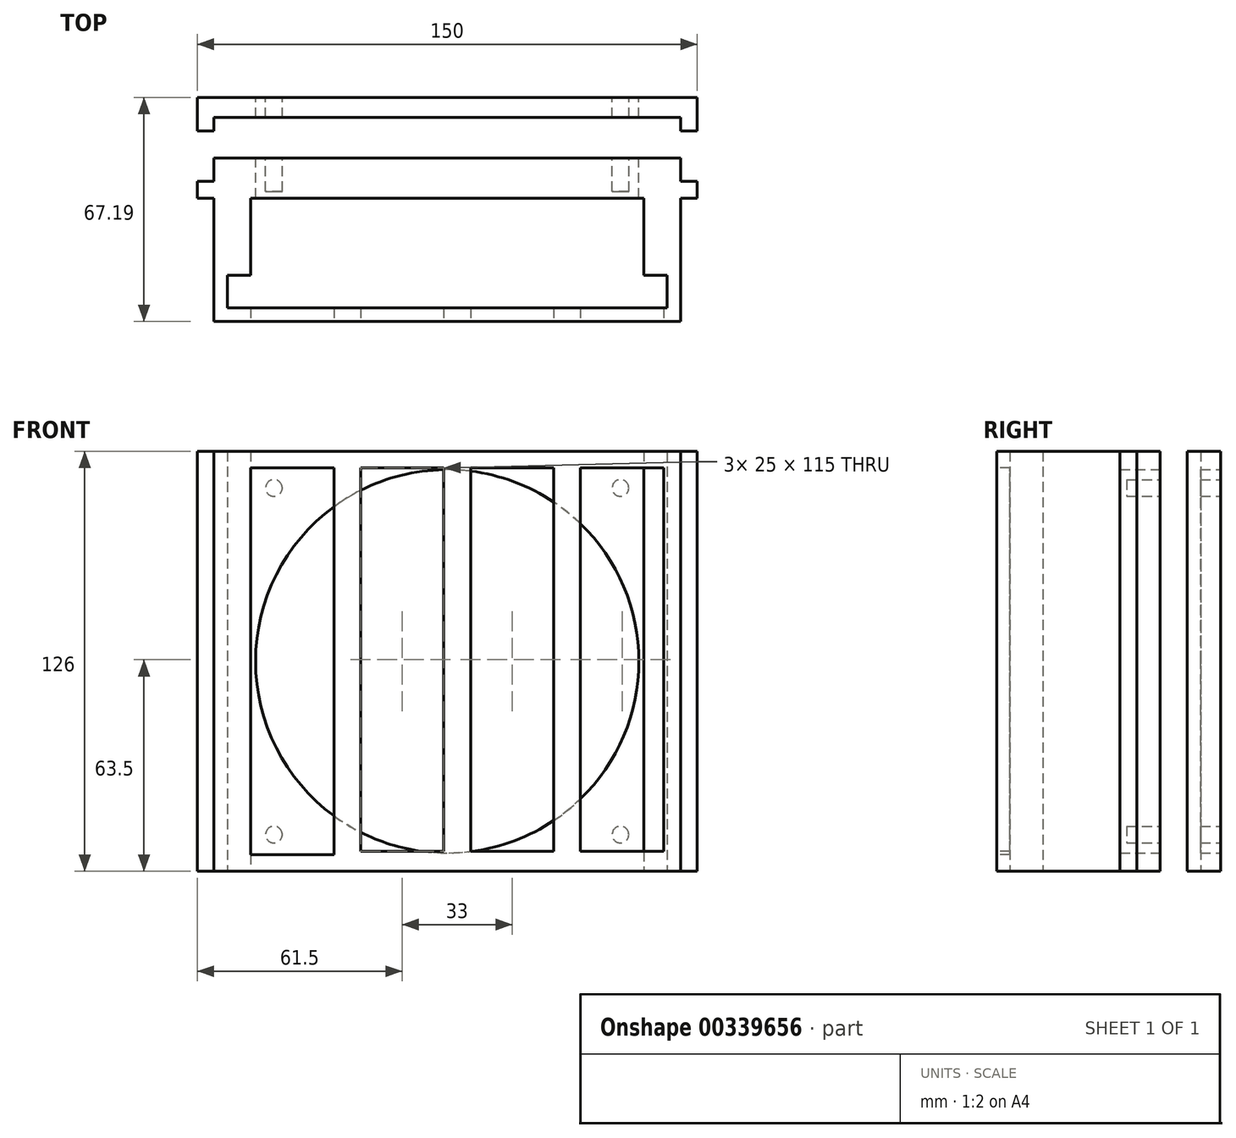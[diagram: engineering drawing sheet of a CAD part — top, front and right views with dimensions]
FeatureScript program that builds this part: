
annotation { "Feature Type Name" : "Feature", "Feature Type Description" : "" }
export const myFeature = defineFeature(function(context is Context, id is Id, definition is map)
    precondition{}
    {
        {
            var Q0;
            Q0=qCreatedBy(makeId("Top.planeOp"),FACE);
            var sketch = newSketch(context, id + "F0", { "sketchPlane" : qUnion([Q0])});
            skLineSegment(sketch, "E0.bottom", {"start": v(-66, 14) * mm, "end": v(66, 14) * mm});
            skLineSegment(sketch, "E0.top", {"start": v(-66, -19) * mm, "end": v(66, -19) * mm});
            skLineSegment(sketch, "E0.left", {"start": v(-66, 14) * mm, "end": v(-66, -19) * mm});
            skLineSegment(sketch, "E0.right", {"start": v(66, 14) * mm, "end": v(66, -19) * mm});
            skLineSegment(sketch, "E1.bottom", {"start": v(-66, -9.2) * mm, "end": v(-59, -9.2) * mm});
            skLineSegment(sketch, "E1.top", {"start": v(-66, 14) * mm, "end": v(-59, 14) * mm});
            skLineSegment(sketch, "E1.left", {"start": v(-66, -9.2) * mm, "end": v(-66, 14) * mm});
            skLineSegment(sketch, "E1.right", {"start": v(-59, -9.2) * mm, "end": v(-59, 14) * mm});
            skLineSegment(sketch, "E2.bottom", {"start": v(66, -9.2) * mm, "end": v(59, -9.2) * mm});
            skLineSegment(sketch, "E2.top", {"start": v(66, 14) * mm, "end": v(59, 14) * mm});
            skLineSegment(sketch, "E2.left", {"start": v(66, -9.2) * mm, "end": v(66, 14) * mm});
            skLineSegment(sketch, "E2.right", {"start": v(59, -9.2) * mm, "end": v(59, 14) * mm});
            skLineSegment(sketch, "E3.bottom", {"start": v(-70, 26) * mm, "end": v(70, 26) * mm});
            skLineSegment(sketch, "E3.top", {"start": v(-70, -23) * mm, "end": v(70, -23) * mm});
            skLineSegment(sketch, "E3.left", {"start": v(-70, 26) * mm, "end": v(-70, -23) * mm});
            skLineSegment(sketch, "E3.right", {"start": v(70, 26) * mm, "end": v(70, -23) * mm});
            skLineSegment(sketch, "E4.bottom", {"start": v(-75, 14) * mm, "end": v(-70, 14) * mm});
            skLineSegment(sketch, "E4.top", {"start": v(-75, 19) * mm, "end": v(-70, 19) * mm});
            skLineSegment(sketch, "E4.left", {"start": v(-75, 14) * mm, "end": v(-75, 19) * mm});
            skLineSegment(sketch, "E4.right", {"start": v(75, 14) * mm, "end": v(75, 19) * mm});
            skLineSegment(sketch, "E5.trimOffspring", {"start": v(70, 14) * mm, "end": v(75, 14) * mm});
            skLineSegment(sketch, "E6.trimOffspring", {"start": v(70, 19) * mm, "end": v(75, 19) * mm});
            skLineSegment(sketch, "E7.bottom", {"start": v(75, 34.19) * mm, "end": v(-75, 34.19) * mm});
            skLineSegment(sketch, "E7.top", {"start": v(75, 44.19) * mm, "end": v(-75, 44.19) * mm});
            skLineSegment(sketch, "E7.left", {"start": v(75, 34.19) * mm, "end": v(75, 44.19) * mm});
            skLineSegment(sketch, "E7.right", {"start": v(-75, 34.19) * mm, "end": v(-75, 44.19) * mm});
            skLineSegment(sketch, "E8.bottom", {"start": v(70, 34.19) * mm, "end": v(-70, 34.19) * mm});
            skLineSegment(sketch, "E8.top", {"start": v(70, 38.19) * mm, "end": v(-70, 38.19) * mm});
            skLineSegment(sketch, "E8.left", {"start": v(70, 34.19) * mm, "end": v(70, 38.19) * mm});
            skLineSegment(sketch, "E8.right", {"start": v(-70, 34.19) * mm, "end": v(-70, 38.19) * mm});
            skSolve(sketch);
        }
        {
            var Q0;
            Q0=makeQuery(id+"F0.imprint","IMPRINT",FACE,{"disambiguationData":[TD([[makeQuery(id+"F0.imprint","IMPRINT",EDGE,{"derivedFrom":sQuery(id+"F0.wireOp",EDGE,"E0.bottom")}),1.0]])]});
            var Q1;
            Q1=makeQuery(id+"F0.imprint","IMPRINT",FACE,{"disambiguationData":[TD([[makeQuery(id+"F0.imprint","IMPRINT",EDGE,{"derivedFrom":sQuery(id+"F0.wireOp",EDGE,"E1.bottom")}),1.0]])]});
            var Q2;
            Q2=makeQuery(id+"F0.imprint","IMPRINT",FACE,{"disambiguationData":[TD([[makeQuery(id+"F0.imprint","IMPRINT",EDGE,{"derivedFrom":sQuery(id+"F0.wireOp",EDGE,"E2.bottom")}),-1.0]])]});
            var Q3;
            {var subQ0=sQuery(id+"F0.wireOp",EDGE,"E4.top");var subQ1=sQuery(id+"F0.wireOp",EDGE,"E3.left");var subQ2=makeQuery(id+"F0.imprint","INTERSECT",VERTEX,{"derivedFrom":[subQ1,subQ0]});Q3=makeQuery(id+"F0.imprint","IMPRINT",FACE,{"disambiguationData":[TD([[makeQuery(id+"F0.imprint","IMPRINT",EDGE,{"disambiguationData":[TD([[subQ2,-1.0]])],"derivedFrom":subQ1}),1.0]])]});}
            var Q4;
            {var subQ0=sQuery(id+"F0.wireOp",EDGE,"E3.bottom");Q4=makeQuery(id+"F0.imprint","IMPRINT",FACE,{"disambiguationData":[TD([[makeQuery(id+"F0.imprint","IMPRINT",EDGE,{"derivedFrom":subQ0}),-1.0]])]});}
            var Q5;
            {var subQ5=sQuery(id+"F0.wireOp",EDGE,"E4.left");Q5=makeQuery(id+"F0.imprint","IMPRINT",FACE,{"disambiguationData":[TD([[makeQuery(id+"F0.imprint","IMPRINT",EDGE,{"derivedFrom":subQ5}),-1.0]])]});}
            var Q6;
            {var subQ5=sQuery(id+"F0.wireOp",EDGE,"E4.right");Q6=makeQuery(id+"F0.imprint","IMPRINT",FACE,{"disambiguationData":[TD([[makeQuery(id+"F0.imprint","IMPRINT",EDGE,{"derivedFrom":subQ5}),1.0]])]});}
            var Q7;
            Q7=makeQuery(id+"F0.imprint","IMPRINT",FACE,{"disambiguationData":[TD([[makeQuery(id+"F0.imprint","IMPRINT",EDGE,{"derivedFrom":sQuery(id+"F0.wireOp",EDGE,"E7.top")}),1.0]])]});
            extrude(context, id + "F1", {"entities" : qUnion([Q0, Q1, Q2, Q3, Q4, Q5, Q6, Q7]), "depth" : 126 * mm});
        }
        {
            var Q0;
            Q0=makeQuery(id+"F1.opExtrude","SWEPT_FACE",FACE,{"disambiguationData":[OSD([sQuery(id+"F0.wireOp",EDGE,"E3.top")])]});
            var sketch = newSketch(context, id + "F2", { "sketchPlane" : qUnion([Q0])});
            skLineSegment(sketch, "E9.bottom", {"start": v(-59, 121) * mm, "end": v(-34, 121) * mm});
            skLineSegment(sketch, "E9.top", {"start": v(-59, 5) * mm, "end": v(-34, 5) * mm});
            skLineSegment(sketch, "E9.left", {"start": v(-59, 121) * mm, "end": v(-59, 5) * mm});
            skLineSegment(sketch, "E9.right", {"start": v(-34, 121) * mm, "end": v(-34, 5) * mm});
            skPoint(sketch, "E10.firstSnap0", {"position": v(-46.5, 121) * mm});
            skLineSegment(sketch, "E10.bottom", {"start": v(65, 121) * mm, "end": v(40, 121) * mm});
            skLineSegment(sketch, "E10.top", {"start": v(65, 6) * mm, "end": v(40, 6) * mm});
            skLineSegment(sketch, "E10.left", {"start": v(65, 121) * mm, "end": v(65, 6) * mm});
            skLineSegment(sketch, "E10.right", {"start": v(40, 121) * mm, "end": v(40, 6) * mm});
            skLineSegment(sketch, "E11.bottom", {"start": v(-26, 121) * mm, "end": v(-1, 121) * mm});
            skLineSegment(sketch, "E11.top", {"start": v(-26, 6) * mm, "end": v(-1, 6) * mm});
            skLineSegment(sketch, "E11.left", {"start": v(-26, 121) * mm, "end": v(-26, 6) * mm});
            skLineSegment(sketch, "E11.right", {"start": v(-1, 121) * mm, "end": v(-1, 6) * mm});
            skLineSegment(sketch, "E12.bottom", {"start": v(7, 121) * mm, "end": v(32, 121) * mm});
            skLineSegment(sketch, "E12.top", {"start": v(7, 6) * mm, "end": v(32, 6) * mm});
            skLineSegment(sketch, "E12.left", {"start": v(7, 121) * mm, "end": v(7, 6) * mm});
            skLineSegment(sketch, "E12.right", {"start": v(32, 121) * mm, "end": v(32, 6) * mm});
            skSolve(sketch);
        }
        {
            var Q0;
            Q0=makeQuery(id+"F2.imprint","IMPRINT",FACE,{"disambiguationData":[TD([[makeQuery(id+"F2.imprint","IMPRINT",EDGE,{"derivedFrom":sQuery(id+"F2.wireOp",EDGE,"E9.bottom")}),-1.0]])]});
            var Q1;
            Q1=makeQuery(id+"F2.imprint","IMPRINT",FACE,{"disambiguationData":[TD([[makeQuery(id+"F2.imprint","IMPRINT",EDGE,{"derivedFrom":sQuery(id+"F2.wireOp",EDGE,"E11.bottom")}),-1.0]])]});
            var Q2;
            Q2=makeQuery(id+"F2.imprint","IMPRINT",FACE,{"disambiguationData":[TD([[makeQuery(id+"F2.imprint","IMPRINT",EDGE,{"derivedFrom":sQuery(id+"F2.wireOp",EDGE,"E12.bottom")}),-1.0]])]});
            var Q3;
            Q3=makeQuery(id+"F2.imprint","IMPRINT",FACE,{"disambiguationData":[TD([[makeQuery(id+"F2.imprint","IMPRINT",EDGE,{"derivedFrom":sQuery(id+"F2.wireOp",EDGE,"E10.bottom")}),1.0]])]});
            extrude(context, id + "F3", {"entities" : qUnion([Q0, Q1, Q2, Q3]), "operationType" : NewBodyOperationType.REMOVE, "oppositeDirection" : true, "depth" : 6 * mm});
        }
        {
            var Q0;
            Q0=makeQuery(id+"F1.opExtrude","SWEPT_FACE",FACE,{"disambiguationData":[OSD([sQuery(id+"F0.wireOp",EDGE,"E3.bottom")])]});
            var sketch = newSketch(context, id + "F4", { "sketchPlane" : qUnion([Q0])});
            skCircle(sketch, "E13", {"center": v(0, 63) * mm, "radius": 57.5 * mm});
            skPoint(sketch, "E13.centerSnap0", {"position": v(-70, 63) * mm});
            skPoint(sketch, "E13.centerSnap1", {"position": v(0, 126) * mm});
            skSolve(sketch);
        }
        {
            var Q0;
            Q0=makeQuery(id+"F4.imprint","IMPRINT",FACE,{"disambiguationData":[TD([[makeQuery(id+"F4.imprint","IMPRINT",EDGE,{"derivedFrom":sQuery(id+"F4.wireOp",EDGE,"E13")}),1.0]])]});
            extrude(context, id + "F5", {"entities" : qUnion([Q0]), "operationType" : NewBodyOperationType.REMOVE, "oppositeDirection" : true, "depth" : 35 * mm, "hasSecondDirection" : true, "secondDirectionOppositeDirection" : false, "secondDirectionDepth" : 25 * mm});
        }
        {
            var Q0;
            Q0=makeQuery(id+"F0.imprint","IMPRINT",FACE,{"disambiguationData":[TD([[makeQuery(id+"F0.imprint","IMPRINT",EDGE,{"derivedFrom":sQuery(id+"F0.wireOp",EDGE,"E0.bottom")}),-1.0]])]});
            extrude(context, id + "F6", {"entities" : qUnion([Q0]), "operationType" : NewBodyOperationType.ADD, "depth" : 5 * mm});
        }
        {
            var Q0;
            Q0=makeQuery(id+"F1.opExtrude","SWEPT_FACE",FACE,{"disambiguationData":[OSD([sQuery(id+"F0.wireOp",EDGE,"E3.bottom")])]});
            var sketch = newSketch(context, id + "F7", { "sketchPlane" : qUnion([Q0])});
            skCircle(sketch, "E14", {"center": v(-52, 115) * mm, "radius": 2.5 * mm});
            skCircle(sketch, "E15", {"center": v(52, 115) * mm, "radius": 2.5 * mm});
            skCircle(sketch, "E16", {"center": v(0, 63) * mm, "radius": 5.64 * mm});
            skCircle(sketch, "E17", {"center": v(-52, 11) * mm, "radius": 2.5 * mm});
            skCircle(sketch, "E18", {"center": v(52, 11) * mm, "radius": 2.5 * mm});
            skSolve(sketch);
        }
        {
            var Q0;
            Q0=makeQuery(id+"F7.imprint","IMPRINT",FACE,{"disambiguationData":[TD([[makeQuery(id+"F7.imprint","IMPRINT",EDGE,{"derivedFrom":sQuery(id+"F7.wireOp",EDGE,"E17")}),1.0]])]});
            var Q1;
            Q1=makeQuery(id+"F7.imprint","IMPRINT",FACE,{"disambiguationData":[TD([[makeQuery(id+"F7.imprint","IMPRINT",EDGE,{"derivedFrom":sQuery(id+"F7.wireOp",EDGE,"E18")}),1.0]])]});
            var Q2;
            Q2=makeQuery(id+"F7.imprint","IMPRINT",FACE,{"disambiguationData":[TD([[makeQuery(id+"F7.imprint","IMPRINT",EDGE,{"derivedFrom":sQuery(id+"F7.wireOp",EDGE,"E15")}),1.0]])]});
            var Q3;
            Q3=makeQuery(id+"F7.imprint","IMPRINT",FACE,{"disambiguationData":[TD([[makeQuery(id+"F7.imprint","IMPRINT",EDGE,{"derivedFrom":sQuery(id+"F7.wireOp",EDGE,"E14")}),1.0]])]});
            extrude(context, id + "F8", {"entities" : qUnion([Q0, Q1, Q2, Q3]), "operationType" : NewBodyOperationType.REMOVE, "oppositeDirection" : true, "depth" : 10 * mm, "hasSecondDirection" : true, "secondDirectionOppositeDirection" : false, "secondDirectionDepth" : 25 * mm});
        }
    });
